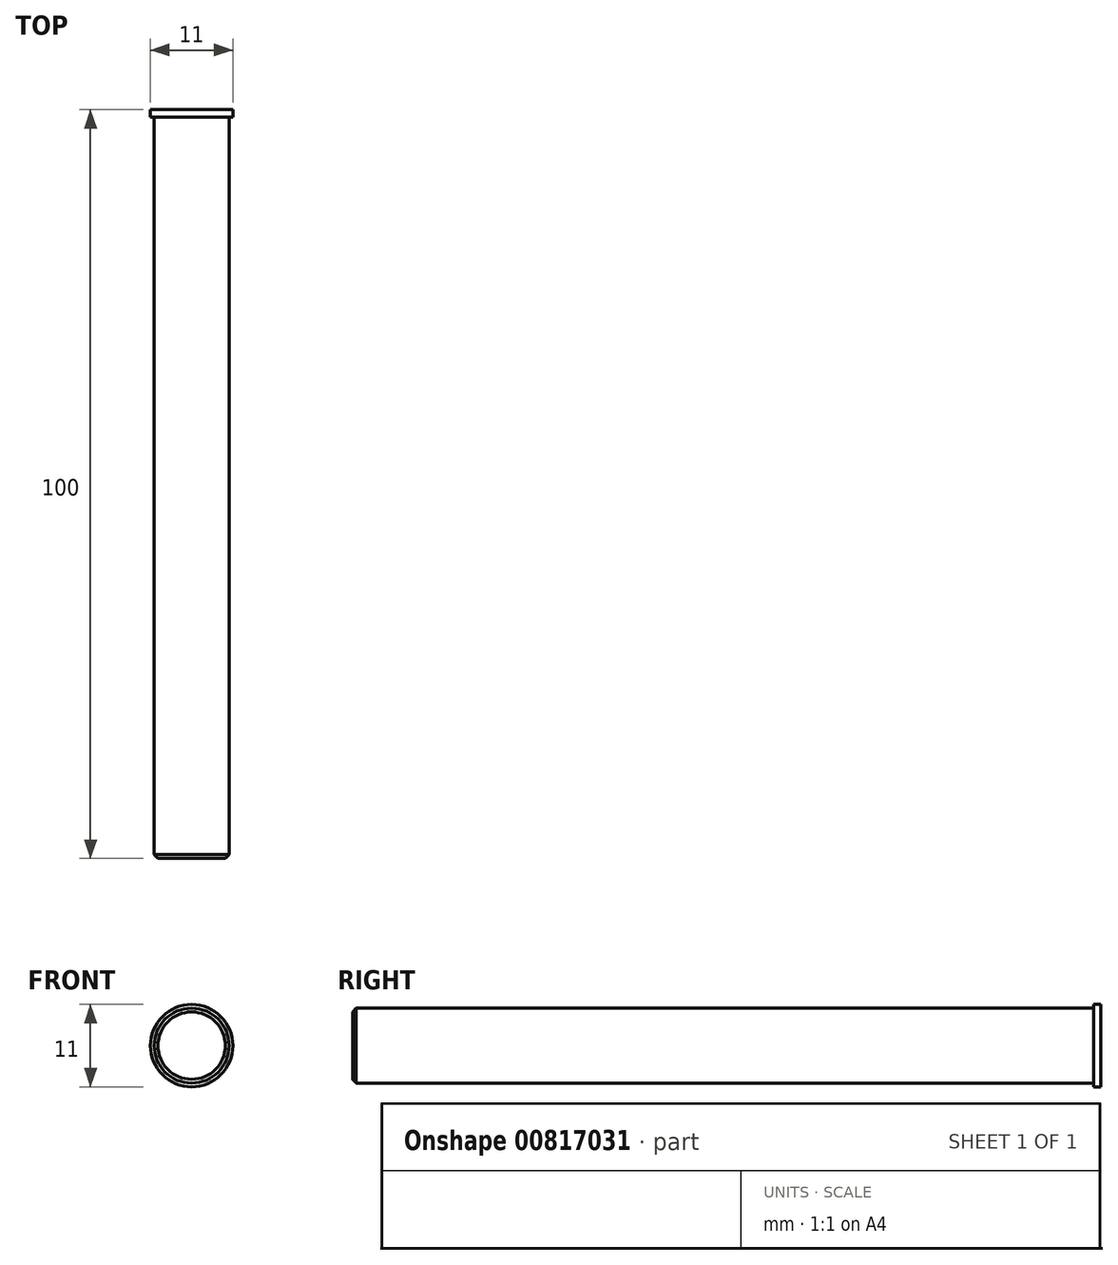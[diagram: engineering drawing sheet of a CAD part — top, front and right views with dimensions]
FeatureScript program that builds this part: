
annotation { "Feature Type Name" : "Feature", "Feature Type Description" : "" }
export const myFeature = defineFeature(function(context is Context, id is Id, definition is map)
    precondition{}
    {
        {
            var Q0;
            Q0=qCreatedBy(makeId("Front.planeOp"),FACE);
            var sketch = newSketch(context, id + "F0", { "sketchPlane" : qUnion([Q0])});
            skCircle(sketch, "E0", {"center": v(0, 0) * mm, "radius": 5 * mm});
            skSolve(sketch);
        }
        {
            var Q0;
            Q0 = qSketchRegion(id + "F0", true);
            extrude(context, id + "F1", {"entities" : qUnion([Q0]), "depth" : 100 * mm, "offsetDistance" : 25 * mm});
        }
        {
            var Q0;
            Q0=makeQuery(id+"F1.opExtrude","CAP_EDGE",EDGE,{"disambiguationData":[OSD([sQuery(id+"F0.wireOp",EDGE,"E0")])],"isStart":false});
            chamfer(context, id + "F2", {"entities" : qUnion([Q0]), "width" : 0.5 * mm, "tangentPropagation" : true});
        }
        {
            var Q0;
            Q0=makeQuery(id+"F1.opExtrude","CAP_FACE",FACE,{"disambiguationData":[OSD([sQuery(id+"F0.wireOp",EDGE,"E0")])],"isStart":true});
            var sketch = newSketch(context, id + "F3", { "sketchPlane" : qUnion([Q0])});
            skCircle(sketch, "E1", {"center": v(0, 0) * mm, "radius": 5.5 * mm});
            skSolve(sketch);
        }
        {
            var Q0;
            Q0 = qSketchRegion(id + "F3", true);
            extrude(context, id + "F4", {"entities" : qUnion([Q0]), "operationType" : NewBodyOperationType.ADD, "oppositeDirection" : true, "depth" : 1 * mm, "offsetDistance" : 25 * mm});
        }
    });
